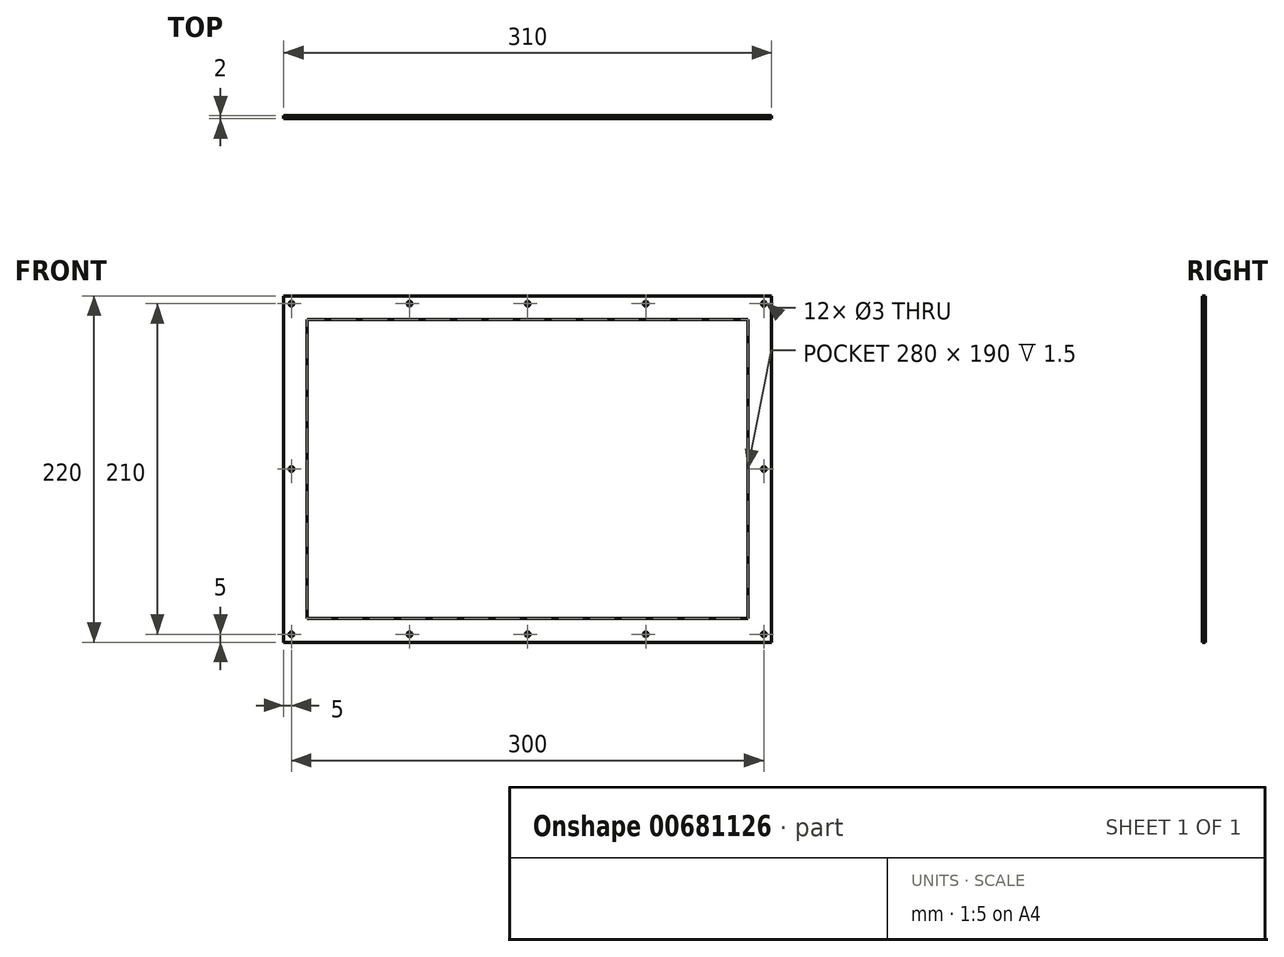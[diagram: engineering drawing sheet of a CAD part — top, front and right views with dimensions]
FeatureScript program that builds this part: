
annotation { "Feature Type Name" : "Feature", "Feature Type Description" : "" }
export const myFeature = defineFeature(function(context is Context, id is Id, definition is map)
    precondition{}
    {
        {
            var Q0;
            Q0=qCreatedBy(makeId("Front.planeOp"),FACE);
            var sketch = newSketch(context, id + "F0", { "sketchPlane" : qUnion([Q0])});
            skLineSegment(sketch, "E0.bottom", {"start": v(-155, -110) * mm, "end": v(155, -110) * mm});
            skLineSegment(sketch, "E0.top", {"start": v(-155, 110) * mm, "end": v(155, 110) * mm});
            skLineSegment(sketch, "E0.left", {"start": v(-155, -110) * mm, "end": v(-155, 110) * mm});
            skLineSegment(sketch, "E0.right", {"start": v(155, -110) * mm, "end": v(155, 110) * mm});
            skPoint(sketch, "E0.middle", {"position": v(0, 0) * mm});
            skPoint(sketch, "E1", {"position": v(-150, 0) * mm});
            skPoint(sketch, "E2", {"position": v(0, 105) * mm});
            skPoint(sketch, "E3", {"position": v(-150, 105) * mm});
            skPoint(sketch, "E4", {"position": v(-75, 105) * mm});
            skPoint(sketch, "E5", {"position": v(0, -105) * mm});
            skPoint(sketch, "E6", {"position": v(-75, -105) * mm});
            skPoint(sketch, "E7", {"position": v(-150, -105) * mm});
            skPoint(sketch, "E8.MirrorP", {"position": v(75, 105) * mm});
            skPoint(sketch, "E9.MirrorP", {"position": v(150, 105) * mm});
            skPoint(sketch, "E10.MirrorP", {"position": v(150, 0) * mm});
            skPoint(sketch, "E11.MirrorP", {"position": v(150, -105) * mm});
            skPoint(sketch, "E12.MirrorP", {"position": v(75, -105) * mm});
            skLineSegment(sketch, "E13.bottom", {"start": v(140, 95) * mm, "end": v(-140, 95) * mm});
            skLineSegment(sketch, "E13.top", {"start": v(140, -95) * mm, "end": v(-140, -95) * mm});
            skLineSegment(sketch, "E13.left", {"start": v(140, 95) * mm, "end": v(140, -95) * mm});
            skLineSegment(sketch, "E13.right", {"start": v(-140, 95) * mm, "end": v(-140, -95) * mm});
            skSolve(sketch);
        }
        {
            var Q0;
            Q0 = qSketchRegion(id + "F0", true);
            extrude(context, id + "F1", {"entities" : qUnion([Q0]), "depth" : 2 * mm, "offsetDistance" : 25 * mm});
        }
        {
            var Q0;
            Q0=sQuery(id+"F0.wireOp",VERTEX,"E3");
            var Q1;
            Q1=sQuery(id+"F0.wireOp",VERTEX,"E4");
            var Q2;
            Q2=sQuery(id+"F0.wireOp",VERTEX,"E2");
            var Q3;
            Q3=sQuery(id+"F0.wireOp",VERTEX,"E8.MirrorP");
            var Q4;
            Q4=sQuery(id+"F0.wireOp",VERTEX,"E9.MirrorP");
            var Q5;
            Q5=sQuery(id+"F0.wireOp",VERTEX,"E10.MirrorP");
            var Q6;
            Q6=sQuery(id+"F0.wireOp",VERTEX,"E11.MirrorP");
            var Q7;
            Q7=sQuery(id+"F0.wireOp",VERTEX,"E12.MirrorP");
            var Q8;
            Q8=sQuery(id+"F0.wireOp",VERTEX,"E5");
            var Q9;
            Q9=sQuery(id+"F0.wireOp",VERTEX,"E6");
            var Q10;
            Q10=sQuery(id+"F0.wireOp",VERTEX,"E7");
            var Q11;
            Q11=sQuery(id+"F0.wireOp",VERTEX,"E1");
            var Q12;
            Q12=makeQuery(id+"F1.opExtrude","SWEPT_BODY",BODY,{"disambiguationData":[OSD([sQuery(id+"F0.wireOp",EDGE,"E0.bottom"),sQuery(id+"F0.wireOp",EDGE,"E0.top"),sQuery(id+"F0.wireOp",EDGE,"E0.left"),sQuery(id+"F0.wireOp",EDGE,"E0.right")])]});
            hole(context, id + "F2", {"style" : HoleStyle.SIMPLE, "endStyle" : HoleEndStyle.THROUGH, "oppositeDirection" : true, "holeDiameter" : 3 * mm, "majorDiameter" : 5 * mm, "isTappedThrough" : true, "tappedDepth" : 12 * mm, "tapClearance" : 3, "startFromSketch" : true, "locations" : qUnion([Q0, Q1, Q2, Q3, Q4, Q5, Q6, Q7, Q8, Q9, Q10, Q11]), "scope" : qUnion([Q12])});
        }
        {
            var Q0;
            Q0=makeQuery(id+"F0.imprint","IMPRINT",FACE,{"disambiguationData":[TD([[makeQuery(id+"F0.imprint","IMPRINT",EDGE,{"derivedFrom":sQuery(id+"F0.wireOp",EDGE,"E13.bottom")}),1.0]])]});
            extrude(context, id + "F3", {"entities" : qUnion([Q0]), "operationType" : NewBodyOperationType.ADD, "depth" : 0.5 * mm, "offsetDistance" : 25 * mm});
        }
    });
